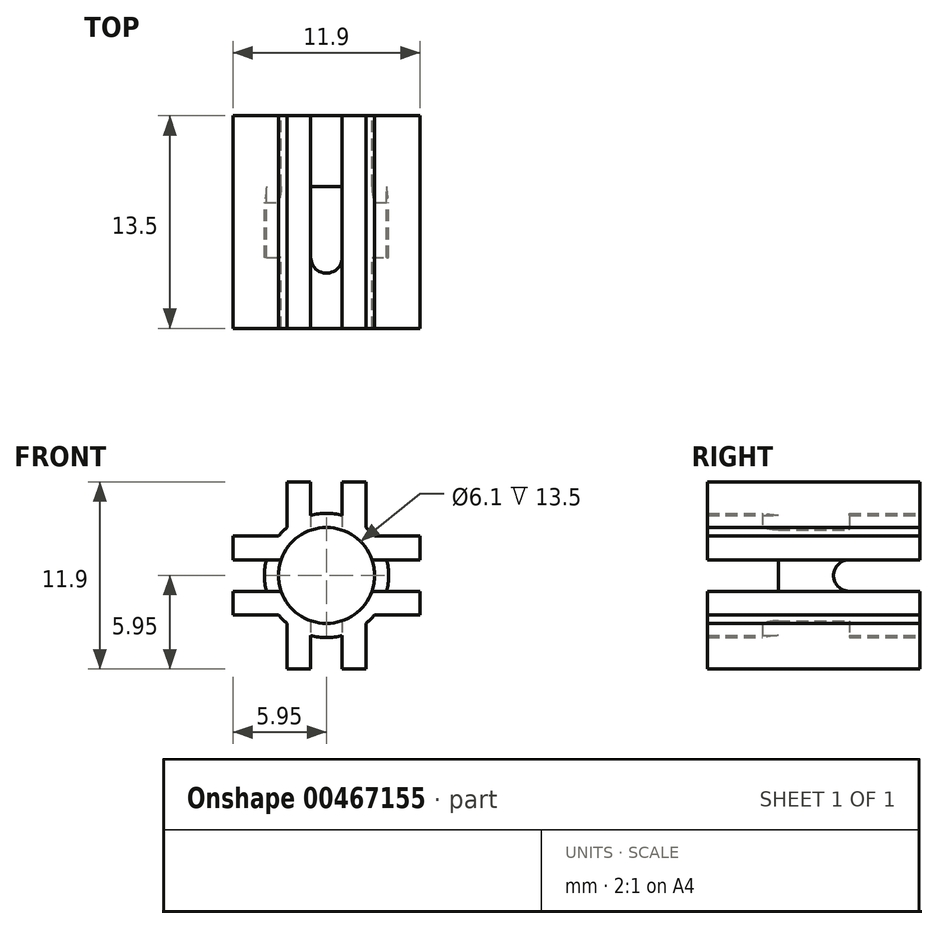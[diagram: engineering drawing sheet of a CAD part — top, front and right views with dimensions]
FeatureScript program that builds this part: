
annotation { "Feature Type Name" : "Feature", "Feature Type Description" : "" }
export const myFeature = defineFeature(function(context is Context, id is Id, definition is map)
    precondition{}
    {
        {
            assignVariable(context, id + "F0", {"name" : "NumberDepth", "anyValue" : 3.5});
        }
        {
            assignVariable(context, id + "F1", {"name" : "SlotLength", "anyValue" : (getVariable(context, 'NumberDepth') + 1) * mm});
        }
        {
            assignVariable(context, id + "F2", {"name" : "CylinderLength", "anyValue" : (getVariable(context, 'SlotLength') * 3)});
        }
        {
            var Q0;
            Q0=qCreatedBy(makeId("Front.planeOp"),FACE);
            var sketch = newSketch(context, id + "F3", { "sketchPlane" : qUnion([Q0])});
            skCircle(sketch, "E0", {"center": v(0, 0) * mm, "radius": 3.05 * mm});
            skCircle(sketch, "E1", {"center": v(0, 0) * mm, "radius": 3.95 * mm});
            skPoint(sketch, "E2.middle", {"position": v(0, 3.95) * mm});
            skLineSegment(sketch, "E3.bottom", {"start": v(-2.5, 5.95) * mm, "end": v(-1, 5.95) * mm});
            skLineSegment(sketch, "E3.top", {"start": v(-2.5, 3.05) * mm, "end": v(-1, 3.05) * mm});
            skLineSegment(sketch, "E3.left", {"start": v(-2.5, 5.95) * mm, "end": v(-2.5, 3.05) * mm});
            skLineSegment(sketch, "E3.right", {"start": v(-1, 5.95) * mm, "end": v(-1, 3.05) * mm});
            skLineSegment(sketch, "E4", {"start": v(0, 7.85) * mm, "end": v(0, -4.38) * mm, "construction": true});
            skLineSegment(sketch, "E5.MirrorCS", {"start": v(2.5, 5.95) * mm, "end": v(1, 5.95) * mm});
            skLineSegment(sketch, "E6.MirrorCS", {"start": v(1, 5.95) * mm, "end": v(1, 3.05) * mm});
            skLineSegment(sketch, "E7.MirrorCS", {"start": v(2.5, 3.05) * mm, "end": v(1, 3.05) * mm});
            skLineSegment(sketch, "E8.MirrorCS", {"start": v(2.5, 5.95) * mm, "end": v(2.5, 3.05) * mm});
            skLineSegment(sketch, "E9.1.0", {"start": v(-3.05, -2.5) * mm, "end": v(-3.05, -1) * mm});
            skLineSegment(sketch, "E9.1.1", {"start": v(-3.05, 2.5) * mm, "end": v(-3.05, 1) * mm});
            skLineSegment(sketch, "E9.1.2", {"start": v(-5.95, -2.5) * mm, "end": v(-5.95, -1) * mm});
            skLineSegment(sketch, "E9.1.3", {"start": v(-5.95, -1) * mm, "end": v(-3.05, -1) * mm});
            skPoint(sketch, "E9.1.4", {"position": v(-3.95, 0) * mm});
            skLineSegment(sketch, "E9.1.5", {"start": v(-5.95, -2.5) * mm, "end": v(-3.05, -2.5) * mm});
            skLineSegment(sketch, "E9.1.6", {"start": v(-5.95, 2.5) * mm, "end": v(-5.95, 1) * mm});
            skLineSegment(sketch, "E9.1.7", {"start": v(-5.95, 1) * mm, "end": v(-3.05, 1) * mm});
            skLineSegment(sketch, "E9.1.8", {"start": v(-5.95, 2.5) * mm, "end": v(-3.05, 2.5) * mm});
            skLineSegment(sketch, "E9.2.0", {"start": v(2.5, -3.05) * mm, "end": v(1, -3.05) * mm});
            skLineSegment(sketch, "E9.2.1", {"start": v(-2.5, -3.05) * mm, "end": v(-1, -3.05) * mm});
            skLineSegment(sketch, "E9.2.2", {"start": v(2.5, -5.95) * mm, "end": v(1, -5.95) * mm});
            skLineSegment(sketch, "E9.2.3", {"start": v(1, -5.95) * mm, "end": v(1, -3.05) * mm});
            skPoint(sketch, "E9.2.4", {"position": v(0, -3.95) * mm});
            skLineSegment(sketch, "E9.2.5", {"start": v(2.5, -5.95) * mm, "end": v(2.5, -3.05) * mm});
            skLineSegment(sketch, "E9.2.6", {"start": v(-2.5, -5.95) * mm, "end": v(-1, -5.95) * mm});
            skLineSegment(sketch, "E9.2.7", {"start": v(-1, -5.95) * mm, "end": v(-1, -3.05) * mm});
            skLineSegment(sketch, "E9.2.8", {"start": v(-2.5, -5.95) * mm, "end": v(-2.5, -3.05) * mm});
            skLineSegment(sketch, "E9.3.0", {"start": v(3.05, 2.5) * mm, "end": v(3.05, 1) * mm});
            skLineSegment(sketch, "E9.3.1", {"start": v(3.05, -2.5) * mm, "end": v(3.05, -1) * mm});
            skLineSegment(sketch, "E9.3.2", {"start": v(5.95, 2.5) * mm, "end": v(5.95, 1) * mm});
            skLineSegment(sketch, "E9.3.3", {"start": v(5.95, 1) * mm, "end": v(3.05, 1) * mm});
            skPoint(sketch, "E9.3.4", {"position": v(3.95, 0) * mm});
            skLineSegment(sketch, "E9.3.5", {"start": v(5.95, 2.5) * mm, "end": v(3.05, 2.5) * mm});
            skLineSegment(sketch, "E9.3.6", {"start": v(5.95, -2.5) * mm, "end": v(5.95, -1) * mm});
            skLineSegment(sketch, "E9.3.7", {"start": v(5.95, -1) * mm, "end": v(3.05, -1) * mm});
            skLineSegment(sketch, "E9.3.8", {"start": v(5.95, -2.5) * mm, "end": v(3.05, -2.5) * mm});
            skSolve(sketch);
        }
        {
            var Q0;
            Q0 = qSketchRegion(id + "F3", true);
            extrude(context, id + "F4", {"entities" : qUnion([Q0]), "endBound" : BoundingType.SYMMETRIC, "depth" : getVariable(context, 'CylinderLength')});
        }
        {
            var Q0;
            Q0=qCreatedBy(makeId("Right.planeOp"),FACE);
            var sketch = newSketch(context, id + "F5", { "sketchPlane" : qUnion([Q0])});
            skLineSegment(sketch, "E10.bottom", {"start": v(-6.75, 1) * mm, "end": v(-2.25, 1) * mm});
            skLineSegment(sketch, "E10.top", {"start": v(-6.75, -1) * mm, "end": v(-2.25, -1) * mm});
            skLineSegment(sketch, "E10.left", {"start": v(-6.75, 1) * mm, "end": v(-6.75, -1) * mm});
            skLineSegment(sketch, "E10.right", {"start": v(-2.25, 1) * mm, "end": v(-2.25, -1) * mm});
            skLineSegment(sketch, "E11", {"start": v(0, 7.97) * mm, "end": v(0, -8) * mm});
            skLineSegment(sketch, "E12.MirrorCS", {"start": v(6.75, -1) * mm, "end": v(2.25, -1) * mm});
            skLineSegment(sketch, "E13.MirrorCS", {"start": v(6.75, 1) * mm, "end": v(6.75, -1) * mm});
            skLineSegment(sketch, "E14.MirrorCS", {"start": v(2.25, 1) * mm, "end": v(2.25, -1) * mm});
            skLineSegment(sketch, "E15.MirrorCS", {"start": v(6.75, 1) * mm, "end": v(2.25, 1) * mm});
            skArc(sketch, "E16", {"start": v(2.25, 1) * mm, "mid": v(1.25, 0) * mm, "end": v(2.25, -1) * mm});
            skSolve(sketch);
        }
        {
            var Q0;
            Q0 = qSketchRegion(id + "F5", true);
            extrude(context, id + "F6", {"entities" : qUnion([Q0]), "operationType" : NewBodyOperationType.REMOVE, "endBound" : BoundingType.SYMMETRIC, "oppositeDirection" : true, "depth" : 10 * mm});
        }
        {
            var Q0;
            Q0=qCreatedBy(makeId("Top.planeOp"),FACE);
            var sketch = newSketch(context, id + "F7", { "sketchPlane" : qUnion([Q0])});
            skLineSegment(sketch, "E17.left", {"start": v(1, -2.25) * mm, "end": v(1, 2.25) * mm});
            skLineSegment(sketch, "E17.right", {"start": v(-1, -2.25) * mm, "end": v(-1, 2.25) * mm});
            skPoint(sketch, "E17.middle", {"position": v(0, 0) * mm});
            skArc(sketch, "E18", {"start": v(-1, -2.25) * mm, "mid": v(0, -3.25) * mm, "end": v(1, -2.25) * mm});
            skLineSegment(sketch, "E19", {"start": v(-1, 2.25) * mm, "end": v(1, 2.25) * mm});
            skSolve(sketch);
        }
        {
            var Q0;
            Q0 = qSketchRegion(id + "F7", true);
            extrude(context, id + "F8", {"entities" : qUnion([Q0]), "operationType" : NewBodyOperationType.REMOVE, "endBound" : BoundingType.SYMMETRIC, "depth" : 25 * mm});
        }
    });
